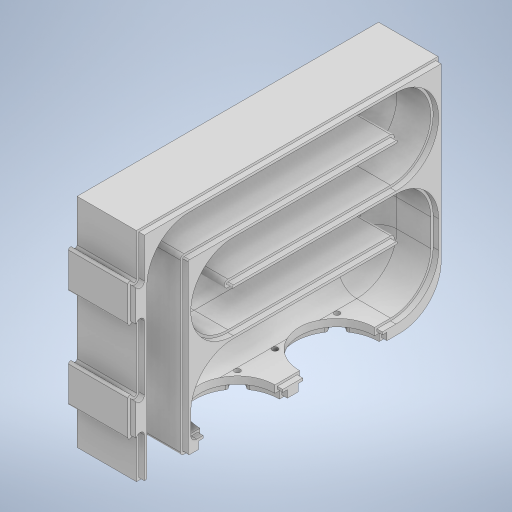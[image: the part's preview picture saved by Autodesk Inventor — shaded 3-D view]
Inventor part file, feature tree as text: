
AUTODESK INVENTOR PART (.ipt)
format: ipt  version: 2023 (Build 270158000, 158)  size: 847,360 bytes
history: native  units: in
note: dims shown in document units (in); Inventor stores cm internally (conversion verified against a paired STEP export)
features: extrude x9, fillet x7, sketch x7, projected_geometry x7, plane x1, split x1
ambient origin geometry x8: Origin, YZ Plane, XZ Plane, XY Plane, X Axis, Y Axis, Z Axis, Center Point
bodies: Solid1 (feature_tree)
feature tree (32):
  extrude  "Extrusion1"  Depth=0.1575in
  extrude  "Extrusion2"  Depth=0.7874in
  extrude  "Extrusion3"  Depth=0.1575in
  fillet  "Fillet1"  Radius=0.1575in
  fillet  "Fillet2"  Radius=0.7874in
  fillet  "Fillet3"  Radius=0.1575in
  fillet  "Fillet4"  Radius=0.7874in
  extrude  "Extrusion4"  Depth=0.1575in
  extrude  "Extrusion5"  Depth=0.1575in
  fillet  "Fillet8"  Radius=0.7874in
  fillet  "Fillet9"  Radius=1.378in
  plane  "Work Plane1"
  extrude  "Extrusion6"  Depth=0.7874in
  split  "Split1"
  extrude  "Extrusion9"  Depth=0.1575in TaperAngle=0.0deg
  fillet  "Fillet10"  Radius=0.0787in
  extrude  "Extrusion10"  Depth=0.0787in
  extrude  "Extrusion11"  Depth=0.3937in
  sketch  "Sketch1"  dims[d10=6.4961in d11=0.1575in]
  sketch  "Sketch2"  dims[d12=4.685in d13=0.0in d18=0.7874in]
  sketch  "Sketch3"  dims[d19=0.1575in d20=0.1575in d21=0.1575in d22=0.7874in d24=0.1575in d25=0.7874in]
  projected_geometry  "Projected Loop1"
  projected_geometry  "Projected Loop2"
  sketch  "Sketch7"  dims[d26=0.7874in d27=0.1575in]
  sketch  "Sketch9"  dims[d28=0.7874in d30=0.1575in d31=0.7874in d32=1.378in]
  projected_geometry  "Projected Loop5"
  sketch  "Sketch10"  dims[d33=0.1575in d34=0.7874in]
  projected_geometry  "Projected Loop6"
  projected_geometry  "Projected Loop7"
  projected_geometry  "Projected Loop8"
  sketch  "Sketch11"  dims[d35=2.2441in d36=0.0in d37=0.1575in d38=0.0in d39=0.0787in d40=0.8661in d41=0.3937in d42=0.3937in d43=1.811in d44=1.811in d45=2.1457in d46=1.2303in d47=2.5591in d48=1.2795in d49=0.1575in d50=0.0in d51=1.6142in d52=1.6142in d53=0.3937in d54=0.0in d58=0.0787in d59=0.9449in d60=-1.2795in d64=0.315in d65=1.378in d66=0.689in d67=0.6299in d68=0.3937in d69=0.0in d96=0.1969in d97=45.0deg d98=45.0deg d99=45.0deg d100=0.7874in d101=0.9843in d102=0.9843in d103=0.7874in d104=4.685in d105=0.0118in d106=0.0118in d107=0.0118in d108=0.0118in d109=0.0118in d110=0.0118in d111=4.685in d112=0.3937in d113=0.0in d114=0.0394in d115=0.0512in d116=0.0512in d117=0.0512in d118=0.1181in d119=0.0in d120=0.0512in d121=0.1181in d122=0.1181in d123=0.5906in d124=0.3937in d125=0.1969in d126=0.1969in d127=0.1969in d128=0.5906in d129=0.1181in d130=0.5906in d131=4.3701in d132=4.9606in d133=3.2283in d134=0.9449in d135=0.748in d136=0.0394in d137=0.0394in d138=0.0394in d139=0.0394in d140=0.0394in d141=0.0394in d142=0.0394in d143=0.0394in d144=0.0394in d145=0.0787in d146=0.0in d148=45.0deg d150=0.9449in d151=0.1181in d152=0.0787in d153=1.5748in d155=360.0deg]
  projected_geometry  "Projected Loop9"
